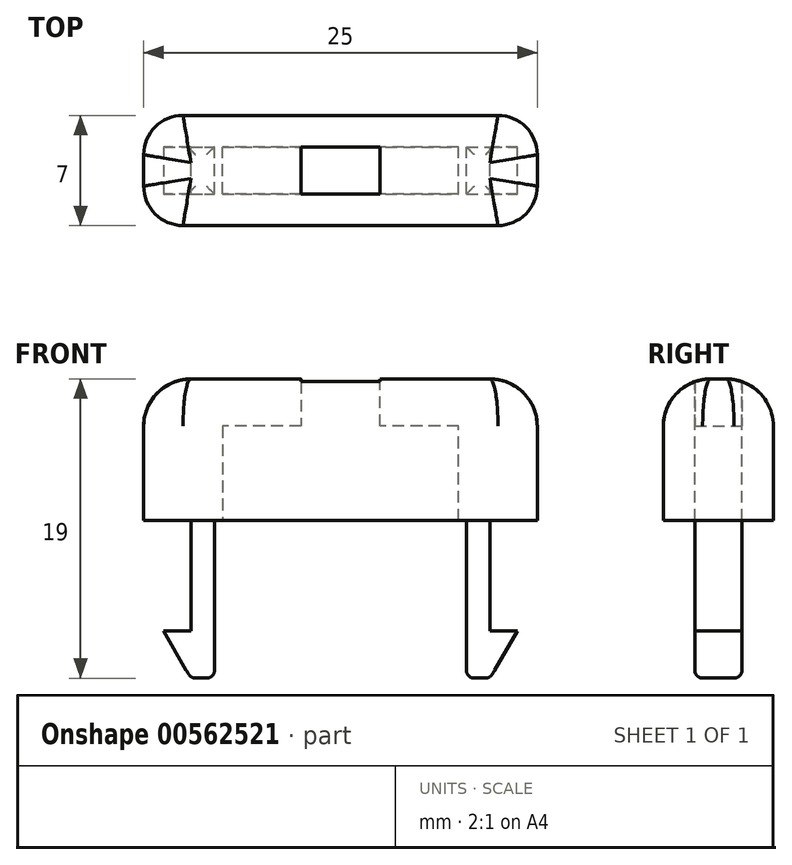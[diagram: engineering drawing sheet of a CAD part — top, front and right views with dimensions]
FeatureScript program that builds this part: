
annotation { "Feature Type Name" : "Feature", "Feature Type Description" : "" }
export const myFeature = defineFeature(function(context is Context, id is Id, definition is map)
    precondition{}
    {
        {
            var Q0;
            Q0=qCreatedBy(makeId("Front.planeOp"),FACE);
            var sketch = newSketch(context, id + "F0", { "sketchPlane" : qUnion([Q0])});
            skLineSegment(sketch, "E0", {"start": v(-16.7, 16.8) * mm, "end": v(-16.7, 13.8) * mm});
            skLineSegment(sketch, "E1", {"start": v(-16.7, 13.8) * mm, "end": v(-21.7, 13.8) * mm});
            skLineSegment(sketch, "E2", {"start": v(-21.7, 13.8) * mm, "end": v(-21.7, 10.8) * mm});
            skLineSegment(sketch, "E3", {"start": v(-21.7, 10.8) * mm, "end": v(-6.7, 10.8) * mm});
            skLineSegment(sketch, "E4", {"start": v(-6.7, 10.8) * mm, "end": v(-6.7, 13.8) * mm});
            skLineSegment(sketch, "E5", {"start": v(-6.7, 13.8) * mm, "end": v(-11.7, 13.8) * mm});
            skLineSegment(sketch, "E6", {"start": v(-11.7, 13.8) * mm, "end": v(-11.7, 16.8) * mm});
            skLineSegment(sketch, "E7", {"start": v(-16.7, 16.8) * mm, "end": v(-26.7, 16.8) * mm});
            skLineSegment(sketch, "E8", {"start": v(-11.7, 16.8) * mm, "end": v(-1.7, 16.8) * mm});
            skLineSegment(sketch, "E9", {"start": v(-26.7, 16.8) * mm, "end": v(-26.7, 7.8) * mm});
            skLineSegment(sketch, "E10", {"start": v(-1.7, 16.8) * mm, "end": v(-1.7, 7.8) * mm});
            skLineSegment(sketch, "E11", {"start": v(-26.7, 7.8) * mm, "end": v(-1.7, 7.8) * mm});
            skSolve(sketch);
        }
        {
            var Q0;
            Q0=makeQuery(id+"F0.imprint","IMPRINT",FACE,{"disambiguationData":[TD([[makeQuery(id+"F0.imprint","IMPRINT",EDGE,{"derivedFrom":sQuery(id+"F0.wireOp",EDGE,"E0")}),-1.0]])]});
            extrude(context, id + "F1", {"entities" : qUnion([Q0]), "depth" : 3 * mm, "offsetDistance" : 25 * mm});
        }
        {
            var Q0;
            Q0=makeQuery(id+"F1.opExtrude","CAP_FACE",FACE,{"disambiguationData":[OSD([sQuery(id+"F0.wireOp",EDGE,"E0"),sQuery(id+"F0.wireOp",EDGE,"E1"),sQuery(id+"F0.wireOp",EDGE,"E2"),sQuery(id+"F0.wireOp",EDGE,"E3"),sQuery(id+"F0.wireOp",EDGE,"E4"),sQuery(id+"F0.wireOp",EDGE,"E5"),sQuery(id+"F0.wireOp",EDGE,"E6"),sQuery(id+"F0.wireOp",EDGE,"E7"),sQuery(id+"F0.wireOp",EDGE,"E8"),sQuery(id+"F0.wireOp",EDGE,"E9"),sQuery(id+"F0.wireOp",EDGE,"E10"),sQuery(id+"F0.wireOp",EDGE,"E11")])],"isStart":false});
            var sketch = newSketch(context, id + "F2", { "sketchPlane" : qUnion([Q0])});
            skLineSegment(sketch, "E12.bottom", {"start": v(-26.7, 16.8) * mm, "end": v(-1.7, 16.8) * mm});
            skLineSegment(sketch, "E12.top", {"start": v(-26.7, 7.8) * mm, "end": v(-1.7, 7.8) * mm});
            skLineSegment(sketch, "E12.left", {"start": v(-26.7, 16.8) * mm, "end": v(-26.7, 7.8) * mm});
            skLineSegment(sketch, "E12.right", {"start": v(-1.7, 16.8) * mm, "end": v(-1.7, 7.8) * mm});
            skSolve(sketch);
        }
        {
            var Q0;
            Q0 = qSketchRegion(id + "F2", true);
            extrude(context, id + "F3", {"entities" : qUnion([Q0]), "operationType" : NewBodyOperationType.ADD, "depth" : 2 * mm, "offsetDistance" : 25 * mm});
        }
        {
            var Q0;
            Q0=makeQuery(id+"F1.opExtrude","CAP_FACE",FACE,{"disambiguationData":[OSD([sQuery(id+"F0.wireOp",EDGE,"E0"),sQuery(id+"F0.wireOp",EDGE,"E1"),sQuery(id+"F0.wireOp",EDGE,"E2"),sQuery(id+"F0.wireOp",EDGE,"E3"),sQuery(id+"F0.wireOp",EDGE,"E4"),sQuery(id+"F0.wireOp",EDGE,"E5"),sQuery(id+"F0.wireOp",EDGE,"E6"),sQuery(id+"F0.wireOp",EDGE,"E7"),sQuery(id+"F0.wireOp",EDGE,"E8"),sQuery(id+"F0.wireOp",EDGE,"E9"),sQuery(id+"F0.wireOp",EDGE,"E10"),sQuery(id+"F0.wireOp",EDGE,"E11")])],"isStart":true});
            var sketch = newSketch(context, id + "F4", { "sketchPlane" : qUnion([Q0])});
            skLineSegment(sketch, "E13.bottom", {"start": v(1.7, 16.8) * mm, "end": v(26.7, 16.8) * mm});
            skLineSegment(sketch, "E13.top", {"start": v(1.7, 7.8) * mm, "end": v(26.7, 7.8) * mm});
            skLineSegment(sketch, "E13.left", {"start": v(1.7, 16.8) * mm, "end": v(1.7, 7.8) * mm});
            skLineSegment(sketch, "E13.right", {"start": v(26.7, 16.8) * mm, "end": v(26.7, 7.8) * mm});
            skSolve(sketch);
        }
        {
            var Q0;
            Q0 = qSketchRegion(id + "F4", true);
            var Q1;
            Q1 = qSketchRegion(id + "F0", true);
            extrude(context, id + "F5", {"entities" : qUnion([Q0, Q1]), "operationType" : NewBodyOperationType.ADD, "depth" : 2 * mm, "offsetDistance" : 25 * mm});
        }
        {
            var Q0;
            {var subQ0=sQuery(id+"F0.wireOp",EDGE,"E11");Q0=makeQuery(id+"F5.boolean.opBoolean","MERGE",FACE,{"derivedFrom":[makeQuery(id+"F3.boolean.opBoolean","MERGE",FACE,{"derivedFrom":[makeQuery(id+"F1.opExtrude","SWEPT_FACE",FACE,{"disambiguationData":[OSD([subQ0])]}),makeQuery(id+"F3.opExtrude","SWEPT_FACE",FACE,{"disambiguationData":[OSD([sQuery(id+"F2.wireOp",EDGE,"E12.top")])]})]}),makeQuery(id+"F5.opExtrude","SWEPT_FACE",FACE,{"disambiguationData":[OSD([subQ0])]})]});}
            var sketch = newSketch(context, id + "F6", { "sketchPlane" : qUnion([Q0])});
            skLineSegment(sketch, "E14", {"start": v(-14.2, -2) * mm, "end": v(-14.2, 0) * mm});
            skLineSegment(sketch, "E15", {"start": v(-14.2, 5) * mm, "end": v(-14.2, 3) * mm});
            skLineSegment(sketch, "E16", {"start": v(-26.7, 1.5) * mm, "end": v(-21.7, 1.5) * mm});
            skLineSegment(sketch, "E17", {"start": v(-1.7, 1.5) * mm, "end": v(-6.7, 1.5) * mm});
            skLineSegment(sketch, "E18.bottom", {"start": v(-21.7, 3) * mm, "end": v(-6.7, 3) * mm});
            skLineSegment(sketch, "E18.top", {"start": v(-21.7, 0) * mm, "end": v(-6.7, 0) * mm});
            skLineSegment(sketch, "E18.left", {"start": v(-21.7, 3) * mm, "end": v(-21.7, 0) * mm});
            skLineSegment(sketch, "E18.right", {"start": v(-6.7, 3) * mm, "end": v(-6.7, 0) * mm});
            skSolve(sketch);
        }
        {
            var Q0;
            Q0 = qSketchRegion(id + "F6", true);
            extrude(context, id + "F7", {"entities" : qUnion([Q0]), "operationType" : NewBodyOperationType.REMOVE, "oppositeDirection" : true, "depth" : 5 * mm, "offsetDistance" : 25 * mm});
        }
        {
            var Q0;
            Q0=makeQuery(id+"F3.opExtrude","CAP_EDGE",EDGE,{"disambiguationData":[OSD([sQuery(id+"F2.wireOp",EDGE,"E12.left")])],"isStart":false});
            var Q1;
            Q1=makeQuery(id+"F5.opExtrude","CAP_EDGE",EDGE,{"disambiguationData":[OSD([sQuery(id+"F0.wireOp",EDGE,"E9")])],"isStart":false});
            var Q2;
            Q2=makeQuery(id+"F5.opExtrude","CAP_EDGE",EDGE,{"disambiguationData":[OSD([sQuery(id+"F0.wireOp",EDGE,"E10")])],"isStart":false});
            var Q3;
            Q3=makeQuery(id+"F3.opExtrude","CAP_EDGE",EDGE,{"disambiguationData":[OSD([sQuery(id+"F2.wireOp",EDGE,"E12.right")])],"isStart":false});
            fillet(context, id + "F8", {"entities" : qUnion([Q0, Q1, Q2, Q3]), "radius" : 2.5 * mm, "tangentPropagation" : true, "allowEdgeOverflow" : false});
        }
        {
            var Q0;
            Q0=makeQuery(id+"F5.boolean.opBoolean","MERGE",EDGE,{"derivedFrom":[makeQuery(id+"F5.opExtrude","CAP_EDGE",EDGE,{"disambiguationData":[OSD([sQuery(id+"F0.wireOp",EDGE,"E7")])],"isStart":false}),makeQuery(id+"F5.opExtrude","CAP_EDGE",EDGE,{"disambiguationData":[OSD([sQuery(id+"F0.wireOp",EDGE,"E8")])],"isStart":false}),makeQuery(id+"F5.opExtrude","CAP_EDGE",EDGE,{"disambiguationData":[OSD([sQuery(id+"F4.wireOp",EDGE,"E13.bottom")])],"isStart":false})]});
            var Q1;
            {var subQ0=sQuery(id+"F0.wireOp",EDGE,"E8");var subQ1=sQuery(id+"F0.wireOp",EDGE,"E7");Q1=makeQuery(id+"F8.opFillet","BLEND_EDGE",EDGE,{"blendedFrom":[makeQuery(id+"F5.opExtrude","CAP_EDGE",EDGE,{"disambiguationData":[OSD([sQuery(id+"F0.wireOp",EDGE,"E10")])],"isStart":false}),makeQuery(id+"F5.boolean.opBoolean","MERGE",FACE,{"derivedFrom":[makeQuery(id+"F3.boolean.opBoolean","MERGE",FACE,{"derivedFrom":[makeQuery(id+"F1.opExtrude","SWEPT_FACE",FACE,{"disambiguationData":[OSD([subQ1])]}),makeQuery(id+"F1.opExtrude","SWEPT_FACE",FACE,{"disambiguationData":[OSD([subQ0])]}),makeQuery(id+"F3.opExtrude","SWEPT_FACE",FACE,{"disambiguationData":[OSD([sQuery(id+"F2.wireOp",EDGE,"E12.bottom")])]})]}),makeQuery(id+"F5.opExtrude","SWEPT_FACE",FACE,{"disambiguationData":[OSD([subQ1])]}),makeQuery(id+"F5.opExtrude","SWEPT_FACE",FACE,{"disambiguationData":[OSD([subQ0])]}),makeQuery(id+"F5.opExtrude","SWEPT_FACE",FACE,{"disambiguationData":[OSD([sQuery(id+"F4.wireOp",EDGE,"E13.bottom")])]})]})],"blendedInto":[makeQuery(id+"F5.boolean.opBoolean","MERGE",FACE,{"derivedFrom":[makeQuery(id+"F3.boolean.opBoolean","MERGE",FACE,{"derivedFrom":[makeQuery(id+"F1.opExtrude","SWEPT_FACE",FACE,{"disambiguationData":[OSD([subQ1])]}),makeQuery(id+"F1.opExtrude","SWEPT_FACE",FACE,{"disambiguationData":[OSD([subQ0])]}),makeQuery(id+"F3.opExtrude","SWEPT_FACE",FACE,{"disambiguationData":[OSD([sQuery(id+"F2.wireOp",EDGE,"E12.bottom")])]})]}),makeQuery(id+"F5.opExtrude","SWEPT_FACE",FACE,{"disambiguationData":[OSD([subQ1])]}),makeQuery(id+"F5.opExtrude","SWEPT_FACE",FACE,{"disambiguationData":[OSD([subQ0])]}),makeQuery(id+"F5.opExtrude","SWEPT_FACE",FACE,{"disambiguationData":[OSD([sQuery(id+"F4.wireOp",EDGE,"E13.bottom")])]})]})]});}
            var Q2;
            {var subQ0=sQuery(id+"F0.wireOp",EDGE,"E8");var subQ1=sQuery(id+"F0.wireOp",EDGE,"E7");Q2=makeQuery(id+"F8.opFillet","BLEND_EDGE",EDGE,{"blendedFrom":[makeQuery(id+"F3.opExtrude","CAP_EDGE",EDGE,{"disambiguationData":[OSD([sQuery(id+"F2.wireOp",EDGE,"E12.right")])],"isStart":false}),makeQuery(id+"F5.boolean.opBoolean","MERGE",FACE,{"derivedFrom":[makeQuery(id+"F3.boolean.opBoolean","MERGE",FACE,{"derivedFrom":[makeQuery(id+"F1.opExtrude","SWEPT_FACE",FACE,{"disambiguationData":[OSD([subQ1])]}),makeQuery(id+"F1.opExtrude","SWEPT_FACE",FACE,{"disambiguationData":[OSD([subQ0])]}),makeQuery(id+"F3.opExtrude","SWEPT_FACE",FACE,{"disambiguationData":[OSD([sQuery(id+"F2.wireOp",EDGE,"E12.bottom")])]})]}),makeQuery(id+"F5.opExtrude","SWEPT_FACE",FACE,{"disambiguationData":[OSD([subQ1])]}),makeQuery(id+"F5.opExtrude","SWEPT_FACE",FACE,{"disambiguationData":[OSD([subQ0])]}),makeQuery(id+"F5.opExtrude","SWEPT_FACE",FACE,{"disambiguationData":[OSD([sQuery(id+"F4.wireOp",EDGE,"E13.bottom")])]})]})],"blendedInto":[makeQuery(id+"F5.boolean.opBoolean","MERGE",FACE,{"derivedFrom":[makeQuery(id+"F3.boolean.opBoolean","MERGE",FACE,{"derivedFrom":[makeQuery(id+"F1.opExtrude","SWEPT_FACE",FACE,{"disambiguationData":[OSD([subQ1])]}),makeQuery(id+"F1.opExtrude","SWEPT_FACE",FACE,{"disambiguationData":[OSD([subQ0])]}),makeQuery(id+"F3.opExtrude","SWEPT_FACE",FACE,{"disambiguationData":[OSD([sQuery(id+"F2.wireOp",EDGE,"E12.bottom")])]})]}),makeQuery(id+"F5.opExtrude","SWEPT_FACE",FACE,{"disambiguationData":[OSD([subQ1])]}),makeQuery(id+"F5.opExtrude","SWEPT_FACE",FACE,{"disambiguationData":[OSD([subQ0])]}),makeQuery(id+"F5.opExtrude","SWEPT_FACE",FACE,{"disambiguationData":[OSD([sQuery(id+"F4.wireOp",EDGE,"E13.bottom")])]})]})]});}
            var Q3;
            {var subQ0=sQuery(id+"F0.wireOp",EDGE,"E10");var subQ1=sQuery(id+"F0.wireOp",EDGE,"E8");Q3=makeQuery(id+"F5.boolean.opBoolean","MERGE",EDGE,{"derivedFrom":[makeQuery(id+"F3.boolean.opBoolean","MERGE",EDGE,{"derivedFrom":[makeQuery(id+"F1.opExtrude","SWEPT_EDGE",EDGE,{"disambiguationData":[OSD([subQ1,subQ0])]}),makeQuery(id+"F3.opExtrude","SWEPT_EDGE",EDGE,{"disambiguationData":[OSD([sQuery(id+"F2.wireOp",EDGE,"E12.bottom"),sQuery(id+"F2.wireOp",EDGE,"E12.right")])]})]}),makeQuery(id+"F5.opExtrude","SWEPT_EDGE",EDGE,{"disambiguationData":[OSD([subQ1,subQ0])]})]});}
            var Q4;
            Q4=makeQuery(id+"F3.opExtrude","CAP_EDGE",EDGE,{"disambiguationData":[OSD([sQuery(id+"F2.wireOp",EDGE,"E12.bottom")])],"isStart":false});
            var Q5;
            {var subQ0=sQuery(id+"F0.wireOp",EDGE,"E8");var subQ1=sQuery(id+"F0.wireOp",EDGE,"E7");Q5=makeQuery(id+"F8.opFillet","BLEND_EDGE",EDGE,{"blendedFrom":[makeQuery(id+"F3.opExtrude","CAP_EDGE",EDGE,{"disambiguationData":[OSD([sQuery(id+"F2.wireOp",EDGE,"E12.left")])],"isStart":false}),makeQuery(id+"F5.boolean.opBoolean","MERGE",FACE,{"derivedFrom":[makeQuery(id+"F3.boolean.opBoolean","MERGE",FACE,{"derivedFrom":[makeQuery(id+"F1.opExtrude","SWEPT_FACE",FACE,{"disambiguationData":[OSD([subQ1])]}),makeQuery(id+"F1.opExtrude","SWEPT_FACE",FACE,{"disambiguationData":[OSD([subQ0])]}),makeQuery(id+"F3.opExtrude","SWEPT_FACE",FACE,{"disambiguationData":[OSD([sQuery(id+"F2.wireOp",EDGE,"E12.bottom")])]})]}),makeQuery(id+"F5.opExtrude","SWEPT_FACE",FACE,{"disambiguationData":[OSD([subQ1])]}),makeQuery(id+"F5.opExtrude","SWEPT_FACE",FACE,{"disambiguationData":[OSD([subQ0])]}),makeQuery(id+"F5.opExtrude","SWEPT_FACE",FACE,{"disambiguationData":[OSD([sQuery(id+"F4.wireOp",EDGE,"E13.bottom")])]})]})],"blendedInto":[makeQuery(id+"F5.boolean.opBoolean","MERGE",FACE,{"derivedFrom":[makeQuery(id+"F3.boolean.opBoolean","MERGE",FACE,{"derivedFrom":[makeQuery(id+"F1.opExtrude","SWEPT_FACE",FACE,{"disambiguationData":[OSD([subQ1])]}),makeQuery(id+"F1.opExtrude","SWEPT_FACE",FACE,{"disambiguationData":[OSD([subQ0])]}),makeQuery(id+"F3.opExtrude","SWEPT_FACE",FACE,{"disambiguationData":[OSD([sQuery(id+"F2.wireOp",EDGE,"E12.bottom")])]})]}),makeQuery(id+"F5.opExtrude","SWEPT_FACE",FACE,{"disambiguationData":[OSD([subQ1])]}),makeQuery(id+"F5.opExtrude","SWEPT_FACE",FACE,{"disambiguationData":[OSD([subQ0])]}),makeQuery(id+"F5.opExtrude","SWEPT_FACE",FACE,{"disambiguationData":[OSD([sQuery(id+"F4.wireOp",EDGE,"E13.bottom")])]})]})]});}
            var Q6;
            {var subQ0=sQuery(id+"F0.wireOp",EDGE,"E9");var subQ1=sQuery(id+"F0.wireOp",EDGE,"E7");Q6=makeQuery(id+"F5.boolean.opBoolean","MERGE",EDGE,{"derivedFrom":[makeQuery(id+"F3.boolean.opBoolean","MERGE",EDGE,{"derivedFrom":[makeQuery(id+"F1.opExtrude","SWEPT_EDGE",EDGE,{"disambiguationData":[OSD([subQ1,subQ0])]}),makeQuery(id+"F3.opExtrude","SWEPT_EDGE",EDGE,{"disambiguationData":[OSD([sQuery(id+"F2.wireOp",EDGE,"E12.bottom"),sQuery(id+"F2.wireOp",EDGE,"E12.left")])]})]}),makeQuery(id+"F5.opExtrude","SWEPT_EDGE",EDGE,{"disambiguationData":[OSD([subQ1,subQ0])]})]});}
            var Q7;
            {var subQ0=sQuery(id+"F0.wireOp",EDGE,"E8");var subQ1=sQuery(id+"F0.wireOp",EDGE,"E7");Q7=makeQuery(id+"F8.opFillet","BLEND_EDGE",EDGE,{"blendedFrom":[makeQuery(id+"F5.opExtrude","CAP_EDGE",EDGE,{"disambiguationData":[OSD([sQuery(id+"F0.wireOp",EDGE,"E9")])],"isStart":false}),makeQuery(id+"F5.boolean.opBoolean","MERGE",FACE,{"derivedFrom":[makeQuery(id+"F3.boolean.opBoolean","MERGE",FACE,{"derivedFrom":[makeQuery(id+"F1.opExtrude","SWEPT_FACE",FACE,{"disambiguationData":[OSD([subQ1])]}),makeQuery(id+"F1.opExtrude","SWEPT_FACE",FACE,{"disambiguationData":[OSD([subQ0])]}),makeQuery(id+"F3.opExtrude","SWEPT_FACE",FACE,{"disambiguationData":[OSD([sQuery(id+"F2.wireOp",EDGE,"E12.bottom")])]})]}),makeQuery(id+"F5.opExtrude","SWEPT_FACE",FACE,{"disambiguationData":[OSD([subQ1])]}),makeQuery(id+"F5.opExtrude","SWEPT_FACE",FACE,{"disambiguationData":[OSD([subQ0])]}),makeQuery(id+"F5.opExtrude","SWEPT_FACE",FACE,{"disambiguationData":[OSD([sQuery(id+"F4.wireOp",EDGE,"E13.bottom")])]})]})],"blendedInto":[makeQuery(id+"F5.boolean.opBoolean","MERGE",FACE,{"derivedFrom":[makeQuery(id+"F3.boolean.opBoolean","MERGE",FACE,{"derivedFrom":[makeQuery(id+"F1.opExtrude","SWEPT_FACE",FACE,{"disambiguationData":[OSD([subQ1])]}),makeQuery(id+"F1.opExtrude","SWEPT_FACE",FACE,{"disambiguationData":[OSD([subQ0])]}),makeQuery(id+"F3.opExtrude","SWEPT_FACE",FACE,{"disambiguationData":[OSD([sQuery(id+"F2.wireOp",EDGE,"E12.bottom")])]})]}),makeQuery(id+"F5.opExtrude","SWEPT_FACE",FACE,{"disambiguationData":[OSD([subQ1])]}),makeQuery(id+"F5.opExtrude","SWEPT_FACE",FACE,{"disambiguationData":[OSD([subQ0])]}),makeQuery(id+"F5.opExtrude","SWEPT_FACE",FACE,{"disambiguationData":[OSD([sQuery(id+"F4.wireOp",EDGE,"E13.bottom")])]})]})]});}
            fillet(context, id + "F9", {"entities" : qUnion([Q0, Q1, Q2, Q3, Q4, Q5, Q6, Q7]), "radius" : 3 * mm, "tangentPropagation" : true, "allowEdgeOverflow" : false});
        }
        {
            var Q0;
            {var subQ0=sQuery(id+"F0.wireOp",EDGE,"E11");Q0=makeQuery(id+"F5.boolean.opBoolean","MERGE",FACE,{"derivedFrom":[makeQuery(id+"F3.boolean.opBoolean","MERGE",FACE,{"derivedFrom":[makeQuery(id+"F1.opExtrude","SWEPT_FACE",FACE,{"disambiguationData":[OSD([subQ0])]}),makeQuery(id+"F3.opExtrude","SWEPT_FACE",FACE,{"disambiguationData":[OSD([sQuery(id+"F2.wireOp",EDGE,"E12.top")])]})]}),makeQuery(id+"F5.opExtrude","SWEPT_FACE",FACE,{"disambiguationData":[OSD([subQ0])]})]});}
            var sketch = newSketch(context, id + "F10", { "sketchPlane" : qUnion([Q0])});
            skLineSegment(sketch, "E19.bottom", {"start": v(-23.7, 3) * mm, "end": v(-22.2, 3) * mm});
            skLineSegment(sketch, "E19.top", {"start": v(-23.7, 0) * mm, "end": v(-22.2, 0) * mm});
            skLineSegment(sketch, "E19.left", {"start": v(-22.2, 3) * mm, "end": v(-22.2, 0) * mm});
            skLineSegment(sketch, "E19.right", {"start": v(-23.7, 3) * mm, "end": v(-23.7, 0) * mm});
            skLineSegment(sketch, "E20.bottom", {"start": v(-6.2, 3) * mm, "end": v(-4.7, 3) * mm});
            skLineSegment(sketch, "E20.top", {"start": v(-6.2, 0) * mm, "end": v(-4.7, 0) * mm});
            skLineSegment(sketch, "E20.left", {"start": v(-6.2, 3) * mm, "end": v(-6.2, 0) * mm});
            skLineSegment(sketch, "E20.right", {"start": v(-4.7, 3) * mm, "end": v(-4.7, 0) * mm});
            skSolve(sketch);
        }
        {
            var Q0;
            Q0=makeQuery(id+"F10.imprint","IMPRINT",FACE,{"disambiguationData":[TD([[makeQuery(id+"F10.imprint","IMPRINT",EDGE,{"derivedFrom":sQuery(id+"F10.wireOp",EDGE,"E19.bottom")}),-1.0]])]});
            var Q1;
            Q1=makeQuery(id+"F10.imprint","IMPRINT",FACE,{"disambiguationData":[TD([[makeQuery(id+"F10.imprint","IMPRINT",EDGE,{"derivedFrom":sQuery(id+"F10.wireOp",EDGE,"E20.bottom")}),-1.0]])]});
            var Q2;
            Q2 = qSketchRegion(id + "F12", true);
            extrude(context, id + "F11", {"entities" : qUnion([Q0, Q1, Q2]), "operationType" : NewBodyOperationType.ADD, "depth" : 10 * mm, "offsetDistance" : 25 * mm});
        }
        {
            var Q0;
            Q0=makeQuery(id+"F11.opExtrude","SWEPT_FACE",FACE,{"disambiguationData":[OSD([sQuery(id+"F10.wireOp",EDGE,"E19.bottom")])]});
            var sketch = newSketch(context, id + "F12", { "sketchPlane" : qUnion([Q0])});
            skLineSegment(sketch, "E21", {"start": v(-23.7, -2.2) * mm, "end": v(-23.7, 0.8) * mm});
            skLineSegment(sketch, "E22", {"start": v(-23.7, 0.8) * mm, "end": v(-25.45, 0.8) * mm});
            skLineSegment(sketch, "E23", {"start": v(-25.45, 0.8) * mm, "end": v(-23.7, -2.2) * mm});
            skSolve(sketch);
        }
        {
            var Q0;
            Q0 = qSketchRegion(id + "F12", true);
            extrude(context, id + "F13", {"entities" : qUnion([Q0]), "operationType" : NewBodyOperationType.ADD, "oppositeDirection" : true, "depth" : 3 * mm, "offsetDistance" : 25 * mm});
        }
        {
            var Q0;
            Q0=makeQuery(id+"F11.opExtrude","SWEPT_FACE",FACE,{"disambiguationData":[OSD([sQuery(id+"F10.wireOp",EDGE,"E20.top")])]});
            var sketch = newSketch(context, id + "F14", { "sketchPlane" : qUnion([Q0])});
            skLineSegment(sketch, "E24", {"start": v(4.7, -2.2) * mm, "end": v(4.7, 0.8) * mm});
            skLineSegment(sketch, "E25", {"start": v(4.7, 0.8) * mm, "end": v(2.95, 0.8) * mm});
            skLineSegment(sketch, "E26", {"start": v(2.95, 0.8) * mm, "end": v(4.7, -2.2) * mm});
            skSolve(sketch);
        }
        {
            var Q0;
            Q0=makeQuery(id+"F14.imprint","IMPRINT",FACE,{"disambiguationData":[TD([[makeQuery(id+"F14.imprint","IMPRINT",EDGE,{"derivedFrom":sQuery(id+"F14.wireOp",EDGE,"E24")}),1.0]])]});
            extrude(context, id + "F15", {"entities" : qUnion([Q0]), "operationType" : NewBodyOperationType.ADD, "oppositeDirection" : true, "depth" : 3 * mm, "offsetDistance" : 25 * mm});
        }
        {
            var Q0;
            Q0=makeQuery(id+"F15.opExtrude","SWEPT_EDGE",EDGE,{"disambiguationData":[OSD([sQuery(id+"F10.wireOp",EDGE,"E20.top"),sQuery(id+"F10.wireOp",EDGE,"E20.right"),sQuery(id+"F14.wireOp",EDGE,"E24"),sQuery(id+"F14.wireOp",EDGE,"E25")])]});
            var Q1;
            Q1=makeQuery(id+"F15.boolean.opBoolean","MERGE",EDGE,{"derivedFrom":[makeQuery(id+"F11.opExtrude","CAP_EDGE",EDGE,{"disambiguationData":[OSD([sQuery(id+"F10.wireOp",EDGE,"E20.right")])],"isStart":false}),makeQuery(id+"F15.opExtrude","SWEPT_EDGE",EDGE,{"disambiguationData":[OSD([sQuery(id+"F10.wireOp",EDGE,"E20.top"),sQuery(id+"F14.wireOp",EDGE,"E24"),sQuery(id+"F14.wireOp",EDGE,"E26")])]})]});
            var Q2;
            Q2=makeQuery(id+"F11.opExtrude","CAP_EDGE",EDGE,{"disambiguationData":[OSD([sQuery(id+"F10.wireOp",EDGE,"E20.bottom")])],"isStart":false});
            var Q3;
            Q3=makeQuery(id+"F11.opExtrude","CAP_EDGE",EDGE,{"disambiguationData":[OSD([sQuery(id+"F10.wireOp",EDGE,"E20.top")])],"isStart":false});
            var Q4;
            Q4=makeQuery(id+"F11.opExtrude","CAP_EDGE",EDGE,{"disambiguationData":[OSD([sQuery(id+"F10.wireOp",EDGE,"E20.left")])],"isStart":false});
            var Q5;
            Q5=makeQuery(id+"F13.opExtrude","SWEPT_EDGE",EDGE,{"disambiguationData":[OSD([sQuery(id+"F10.wireOp",EDGE,"E19.bottom"),sQuery(id+"F10.wireOp",EDGE,"E19.right"),sQuery(id+"F12.wireOp",EDGE,"E21"),sQuery(id+"F12.wireOp",EDGE,"E22")])]});
            var Q6;
            Q6=makeQuery(id+"F11.opExtrude","CAP_EDGE",EDGE,{"disambiguationData":[OSD([sQuery(id+"F10.wireOp",EDGE,"E19.top")])],"isStart":false});
            var Q7;
            Q7=makeQuery(id+"F11.opExtrude","CAP_EDGE",EDGE,{"disambiguationData":[OSD([sQuery(id+"F10.wireOp",EDGE,"E19.left")])],"isStart":false});
            var Q8;
            Q8=makeQuery(id+"F11.opExtrude","CAP_EDGE",EDGE,{"disambiguationData":[OSD([sQuery(id+"F10.wireOp",EDGE,"E19.bottom")])],"isStart":false});
            var Q9;
            Q9=makeQuery(id+"F13.boolean.opBoolean","MERGE",EDGE,{"derivedFrom":[makeQuery(id+"F11.opExtrude","CAP_EDGE",EDGE,{"disambiguationData":[OSD([sQuery(id+"F10.wireOp",EDGE,"E19.right")])],"isStart":false}),makeQuery(id+"F13.opExtrude","SWEPT_EDGE",EDGE,{"disambiguationData":[OSD([sQuery(id+"F10.wireOp",EDGE,"E19.bottom"),sQuery(id+"F12.wireOp",EDGE,"E21"),sQuery(id+"F12.wireOp",EDGE,"E23")])]})]});
            fillet(context, id + "F16", {"entities" : qUnion([Q0, Q1, Q2, Q3, Q4, Q5, Q6, Q7, Q8, Q9]), "radius" : .5 * mm, "tangentPropagation" : true, "allowEdgeOverflow" : false});
        }
    });
